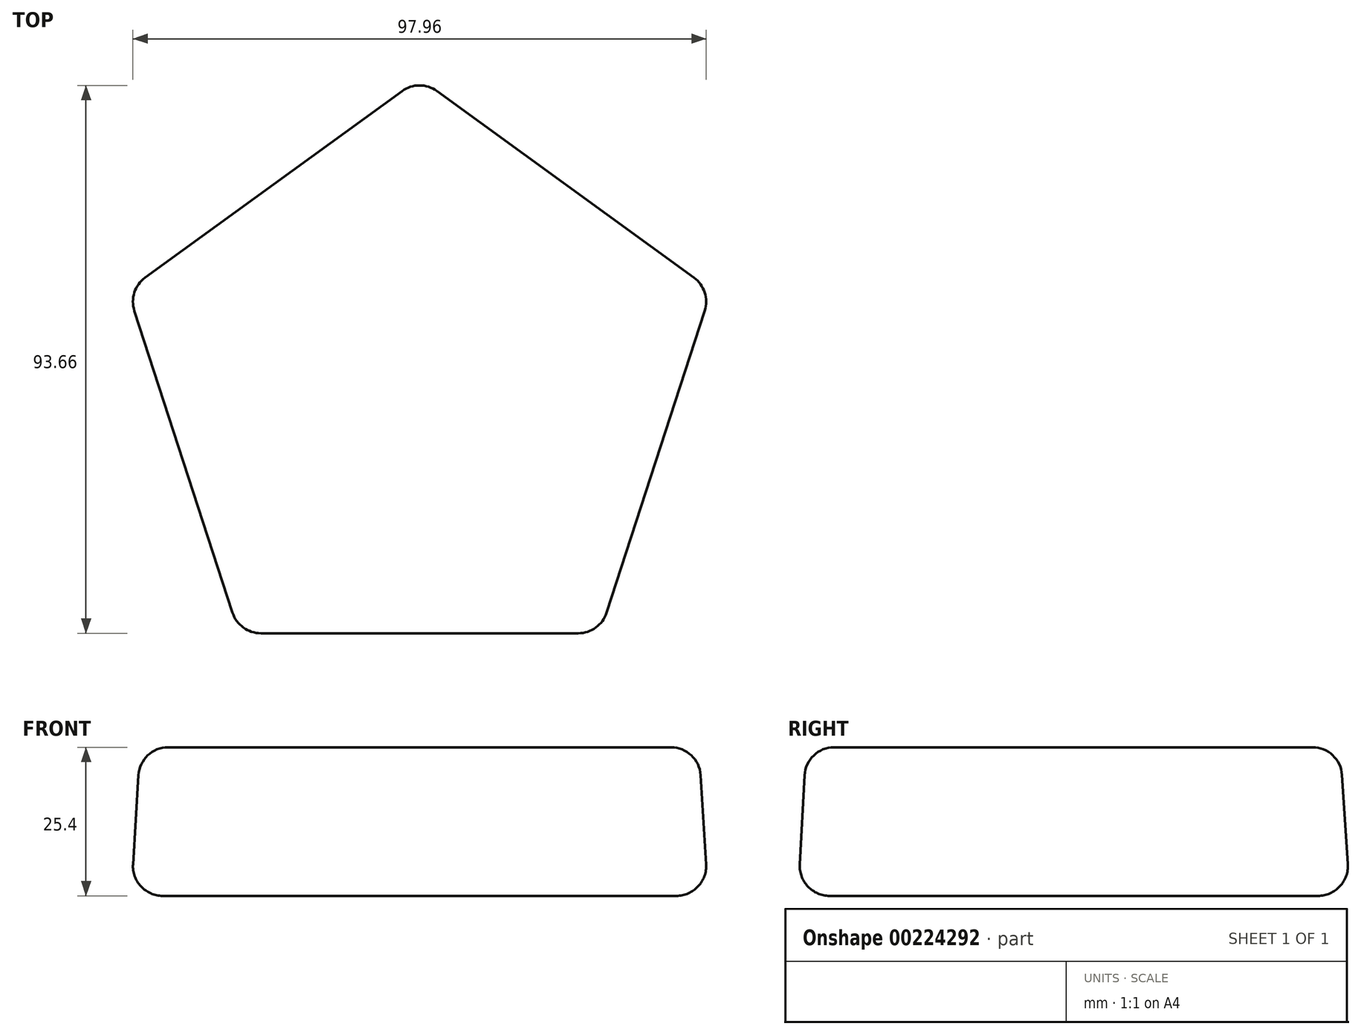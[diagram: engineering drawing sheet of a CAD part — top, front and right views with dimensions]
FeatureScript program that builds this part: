
annotation { "Feature Type Name" : "Feature", "Feature Type Description" : "" }
export const myFeature = defineFeature(function(context is Context, id is Id, definition is map)
    precondition{}
    {
        {
            var Q0;
            Q0=qCreatedBy(makeId("Top.planeOp"),FACE);
            var sketch = newSketch(context, id + "F0", { "sketchPlane" : qUnion([Q0])});
            skCircle(sketch, "E0.cCircle", {"center": v(0, 0) * mm, "radius": 42.7 * mm, "construction": true});
            skLineSegment(sketch, "E0.0", {"start": v(-50.2, 16.3) * mm, "end": v(0, 52.78) * mm});
            skLineSegment(sketch, "E0.1", {"start": v(0, 52.78) * mm, "end": v(50.2, 16.3) * mm});
            skLineSegment(sketch, "E0.2", {"start": v(50.2, 16.3) * mm, "end": v(31.02, -42.7) * mm});
            skLineSegment(sketch, "E0.3", {"start": v(31.02, -42.7) * mm, "end": v(-31.02, -42.7) * mm});
            skLineSegment(sketch, "E0.4", {"start": v(-31.02, -42.7) * mm, "end": v(-50.2, 16.3) * mm});
            skPoint(sketch, "E0.0.midPoint", {"position": v(-25.1, 34.54) * mm});
            skSolve(sketch);
        }
        {
            var Q0;
            Q0 = qSketchRegion(id + "F0", true);
            extrude(context, id + "F1", {"entities" : qUnion([Q0]), "depth" : 25.4 * mm, "hasDraft" : true, "draftAngle" : 3 * degree, "draftPullDirection" : true});
        }
        {
            var Q0;
            Q0=makeQuery(id+"F1.opExtrude","CAP_FACE",FACE,{"disambiguationData":[OSD([sQuery(id+"F0.wireOp",EDGE,"E0.0"),sQuery(id+"F0.wireOp",EDGE,"E0.1"),sQuery(id+"F0.wireOp",EDGE,"E0.2"),sQuery(id+"F0.wireOp",EDGE,"E0.3"),sQuery(id+"F0.wireOp",EDGE,"E0.4")])],"isStart":false});
            var Q1;
            Q1=makeQuery(id+"F1.opExtrude","CAP_FACE",FACE,{"disambiguationData":[OSD([sQuery(id+"F0.wireOp",EDGE,"E0.0"),sQuery(id+"F0.wireOp",EDGE,"E0.1"),sQuery(id+"F0.wireOp",EDGE,"E0.2"),sQuery(id+"F0.wireOp",EDGE,"E0.3"),sQuery(id+"F0.wireOp",EDGE,"E0.4")])],"isStart":true});
            var Q2;
            Q2=makeQuery(id+"F1.opExtrude","SWEPT_FACE",FACE,{"disambiguationData":[OSD([sQuery(id+"F0.wireOp",EDGE,"E0.2")])]});
            var Q3;
            Q3=makeQuery(id+"F1.opExtrude","SWEPT_FACE",FACE,{"disambiguationData":[OSD([sQuery(id+"F0.wireOp",EDGE,"E0.3")])]});
            var Q4;
            Q4=makeQuery(id+"F1.opExtrude","SWEPT_FACE",FACE,{"disambiguationData":[OSD([sQuery(id+"F0.wireOp",EDGE,"E0.1")])]});
            var Q5;
            Q5=makeQuery(id+"F1.opExtrude","SWEPT_FACE",FACE,{"disambiguationData":[OSD([sQuery(id+"F0.wireOp",EDGE,"E0.0")])]});
            var Q6;
            Q6=makeQuery(id+"F1.opExtrude","SWEPT_FACE",FACE,{"disambiguationData":[OSD([sQuery(id+"F0.wireOp",EDGE,"E0.4")])]});
            fillet(context, id + "F2", {"entities" : qUnion([Q0, Q1, Q2, Q3, Q4, Q5, Q6]), "radius" : 5.08 * mm, "tangentPropagation" : true, "allowEdgeOverflow" : false});
        }
    });
